# Revit family: Chair-Soft_Seating-Allermuir-Bison
name_source: partatom
category: Furniture
revit_build: Autodesk Revit Architecture 2012 (Build: 20110309_2315(x64)
units: mm (PartAtom-declared; Revit-internal decimal feet)

## types (1)
- BN1 - Tub chair
    04 CSI = 12 51 00
    95 CSI = 12510
    Arm Height = 2' - 6 5/16"
    Assembly Code = E2020200
    Brochure URL = http://www.allermuir.net
    CAD Blocks URL = http://www.allermuir.net
    Color Availability = See price list for material options
    Description = Tub chair
    Fabric Spec Sheets = http://www.allermuir.net
    LEED Stats URL = http://www.allermuir.net
    Manufacturer = Allermuir
    Manufacturer Fax = (419) 887 5805
    Model = BN1
    Overall Depth = 1' - 10 3/4"
    Overall Height = 2' - 7 3/4"
    Overall Width = 2' - 0 1/2"
    Plugin Data URL = http://products.ecoscorecard.com
    Pricing URL = http://www.allermuir.net
    Product Line = Bison
    Product Page URL = http://www.allermuir.net
    Seat Depth = 1' - 6"
    Seat Height = 1' - 6 3/4"
    Seat Width = 1' - 8 7/8"
    Seat or Base = Fabric - Allermuir - Silcoates
    Specifications URL = http://www.allermuir.net
    Stacks = Yes
    Stand = Metal - Allermuir - Silver
    Subcategory = Soft Seating
    URL = http://www.allermuir.net
    Weight = 55.0 lb
    ecoScorecard Product Page = http://products.ecoscorecard.com
    ecoScorecard_data = http://thesenatorgroup.ecoscorecard.com

## geometry (parser evidence)
native form markers: Sweep x5
no freeform markers — native parametric forms only
